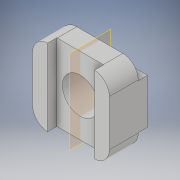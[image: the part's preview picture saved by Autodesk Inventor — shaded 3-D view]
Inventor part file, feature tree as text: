
AUTODESK INVENTOR PART (.ipt)
format: ipt  version: 2018 (Build 220112000, 112)  size: 137,728 bytes
history: native  units: in
note: dims shown in document units (in); Inventor stores cm internally (conversion verified against a paired STEP export)
features: extrude x3, sketch x3, fillet x1
ambient origin geometry x8: Origin, YZ Plane, XZ Plane, XY Plane, X Axis, Y Axis, Z Axis, Center Point
bodies: Solid1 (feature_tree)
feature tree (7):
  extrude  "Extrusion1"  Depth=1.5748in
  extrude  "Extrusion2"  Depth=0.9252in
  fillet  "Fillet1"  Radius=1.5748in
  extrude  "Extrusion3"  Depth=0.189in
  sketch  "Sketch1"  dims[d0=0.5906in d1=1.5748in]
  sketch  "Sketch2"  dims[d2=0.189in d3=0.9252in d4=1.5748in d5=0.0in]
  sketch  "Sketch3"  dims[d6=0.9606in d7=0.189in d8=1.5748in d9=0.0in d10=0.315in d11=0.7323in d12=1.5748in d13=0.0in]
